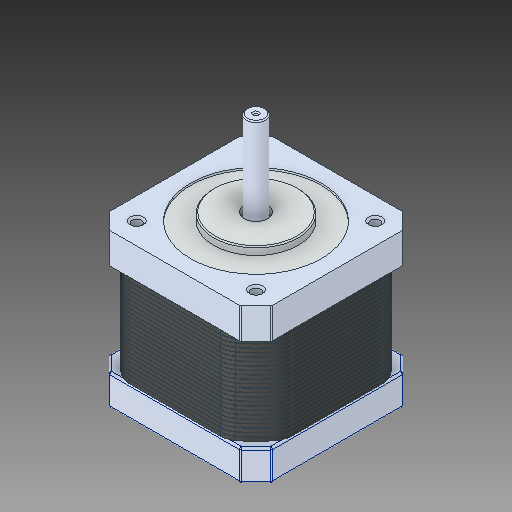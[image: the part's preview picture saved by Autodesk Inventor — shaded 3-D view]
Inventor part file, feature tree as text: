
AUTODESK INVENTOR PART (.ipt)
format: ipt  version: 2019 (Build 230136000, 136)  size: 1,056,768 bytes
history: mixed  units: in
note: dims shown in document units (in); Inventor stores cm internally (conversion verified against a paired STEP export)
features: chamfer x26, fillet x1, imported_body x1
ambient origin geometry x8: Origin, YZ Plane, XZ Plane, XY Plane, X Axis, Y Axis, Z Axis, Center Point
bodies: Solid1 (imported_parasolid), Solid2 (imported_parasolid), Solid3 (imported_parasolid), Solid4 (imported_parasolid), Solid5 (imported_parasolid), Solid6 (imported_parasolid), Solid7 (imported_parasolid), Solid8 (imported_parasolid), Solid9 (imported_parasolid), Solid10 (imported_parasolid), Solid11 (imported_parasolid), Solid12 (imported_parasolid), Solid13 (imported_parasolid), Solid14 (imported_parasolid), Solid15 (imported_parasolid), Solid16 (imported_parasolid), Solid17 (imported_parasolid), Solid18 (imported_parasolid), Solid19 (imported_parasolid), Solid20 (imported_parasolid), Solid21 (imported_parasolid), Solid22 (imported_parasolid), Solid23 (imported_parasolid), Solid24 (imported_parasolid), Solid25 (imported_parasolid), Solid26 (imported_parasolid), Solid27 (imported_parasolid)
feature tree (28):
  fillet  "Redondeo1"  [1 undecoded]
  chamfer  "Chaflán1"  [1 undecoded]
  chamfer  "Chaflán5"  [1 undecoded]
  chamfer  "Chaflán6"  [1 undecoded]
  chamfer  "Chaflán7"  [1 undecoded]
  chamfer  "Chaflán8"  [1 undecoded]
  chamfer  "Chaflán9"  [1 undecoded]
  chamfer  "Chaflán10"  [1 undecoded]
  chamfer  "Chaflán11"  [1 undecoded]
  chamfer  "Chaflán12"  [1 undecoded]
  chamfer  "Chaflán13"  [1 undecoded]
  chamfer  "Chaflán14"  [1 undecoded]
  chamfer  "Chaflán15"  [1 undecoded]
  chamfer  "Chaflán16"  [1 undecoded]
  chamfer  "Chaflán17"  [1 undecoded]
  chamfer  "Chaflán18"  [1 undecoded]
  chamfer  "Chaflán19"  [1 undecoded]
  chamfer  "Chaflán20"  [1 undecoded]
  chamfer  "Chaflán21"  [1 undecoded]
  chamfer  "Chaflán22"  [1 undecoded]
  chamfer  "Chaflán23"  [1 undecoded]
  chamfer  "Chaflán24"  [1 undecoded]
  chamfer  "Chaflán25"  [1 undecoded]
  chamfer  "Chaflán26"  [1 undecoded]
  chamfer  "Chaflán27"  [1 undecoded]
  chamfer  "Chaflán28"  [1 undecoded]
  chamfer  "Chaflán29"  [1 undecoded]
  imported_body  NMx_Import_Brep_tag  [imported B-rep: ~1302 faces, bbox_mm=[42.3, 64.2, 42.3]]
note: 27 required parameter values undecoded (feature->parameter linkage not recoverable at this tier; creation-order binding heuristic only, values carry confidence <= 0.55)
